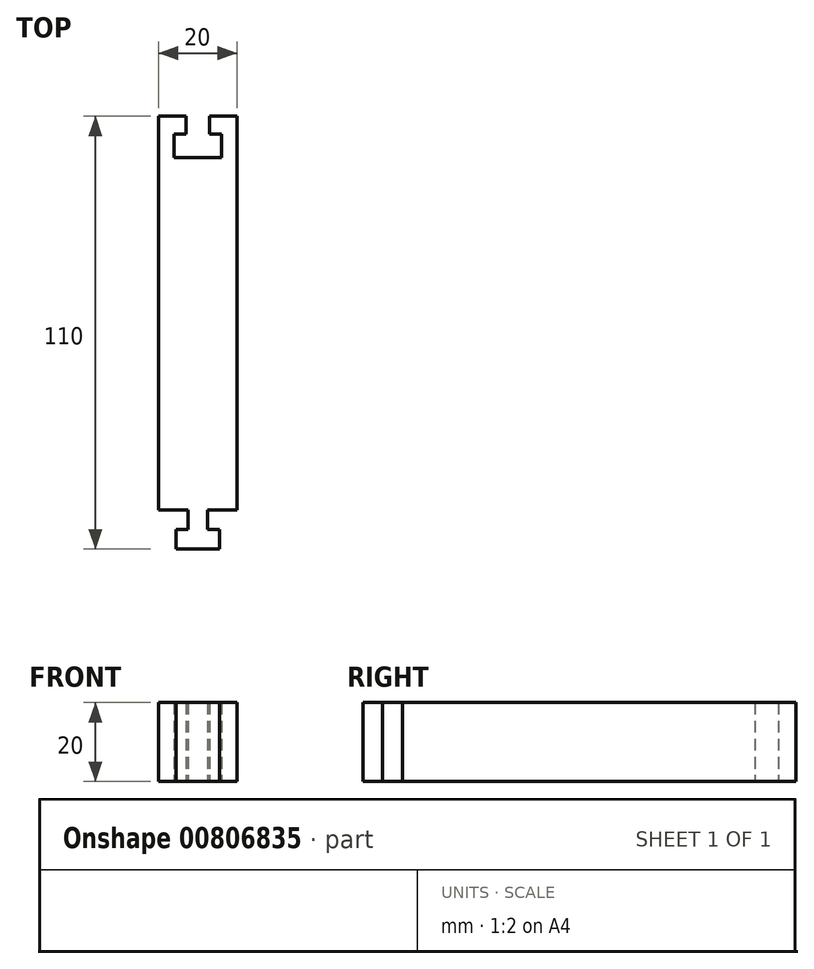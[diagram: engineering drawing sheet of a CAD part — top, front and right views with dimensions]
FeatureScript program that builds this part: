
annotation { "Feature Type Name" : "Feature", "Feature Type Description" : "" }
export const myFeature = defineFeature(function(context is Context, id is Id, definition is map)
    precondition{}
    {
        {
            var Q0;
            Q0=qCreatedBy(makeId("Top.planeOp"),FACE);
            var sketch = newSketch(context, id + "F0", { "sketchPlane" : qUnion([Q0])});
            skLineSegment(sketch, "E0.bottom", {"start": v(10, 50) * mm, "end": v(-10, 50) * mm});
            skLineSegment(sketch, "E0.top", {"start": v(10, -50) * mm, "end": v(-10, -50) * mm});
            skLineSegment(sketch, "E0.left", {"start": v(10, 50) * mm, "end": v(10, -50) * mm});
            skLineSegment(sketch, "E0.right", {"start": v(-10, 50) * mm, "end": v(-10, -50) * mm});
            skPoint(sketch, "E0.middle", {"position": v(0, 0) * mm});
            skLineSegment(sketch, "E1.bottom", {"start": v(3, 42.5) * mm, "end": v(-3, 42.5) * mm});
            skLineSegment(sketch, "E1.top", {"start": v(3, 57.5) * mm, "end": v(-3, 57.5) * mm});
            skLineSegment(sketch, "E1.left", {"start": v(3, 42.5) * mm, "end": v(3, 57.5) * mm});
            skLineSegment(sketch, "E1.right", {"start": v(-3, 42.5) * mm, "end": v(-3, 57.5) * mm});
            skPoint(sketch, "E1.middle", {"position": v(0, 50) * mm});
            skPoint(sketch, "E2.middle", {"position": v(0, -50) * mm});
            skLineSegment(sketch, "E3.bottom", {"start": v(-10, 50) * mm, "end": v(10, 50) * mm});
            skLineSegment(sketch, "E3.left", {"start": v(-10, 50) * mm, "end": v(-10, 35) * mm});
            skLineSegment(sketch, "E3.right", {"start": v(10, 50) * mm, "end": v(10, 35) * mm});
            skLineSegment(sketch, "E4.bottom", {"start": v(-10, -50) * mm, "end": v(10, -50) * mm});
            skLineSegment(sketch, "E4.left", {"start": v(-10, -50) * mm, "end": v(-10, -32.12) * mm});
            skLineSegment(sketch, "E4.right", {"start": v(10, -50) * mm, "end": v(10, -32.12) * mm});
            skLineSegment(sketch, "E5.bottom", {"start": v(6, 39.5) * mm, "end": v(-6, 39.5) * mm});
            skLineSegment(sketch, "E5.top", {"start": v(6, 45.5) * mm, "end": v(-6, 45.5) * mm});
            skLineSegment(sketch, "E5.left", {"start": v(6, 39.5) * mm, "end": v(6, 45.5) * mm});
            skLineSegment(sketch, "E5.right", {"start": v(-6, 39.5) * mm, "end": v(-6, 45.5) * mm});
            skPoint(sketch, "E5.middle", {"position": v(0, 42.5) * mm});
            skLineSegment(sketch, "E6.top", {"start": v(-10, 39.5) * mm, "end": v(10, 39.5) * mm});
            skLineSegment(sketch, "E6.left", {"start": v(-10, 50) * mm, "end": v(-10, 39.5) * mm});
            skLineSegment(sketch, "E6.right", {"start": v(10, 50) * mm, "end": v(10, 39.5) * mm});
            skLineSegment(sketch, "E7.left", {"start": v(-10, -50) * mm, "end": v(-10, -39.5) * mm});
            skLineSegment(sketch, "E7.right", {"start": v(10, -50) * mm, "end": v(10, -39.5) * mm});
            skLineSegment(sketch, "E8.bottom", {"start": v(-5.75, -50) * mm, "end": v(5.75, -50) * mm});
            skLineSegment(sketch, "E9.bottom", {"start": v(2.5, -57.5) * mm, "end": v(-2.5, -57.5) * mm});
            skLineSegment(sketch, "E9.top", {"start": v(2.5, -42.5) * mm, "end": v(-2.5, -42.5) * mm});
            skLineSegment(sketch, "E9.left", {"start": v(2.5, -57.5) * mm, "end": v(2.5, -42.5) * mm});
            skLineSegment(sketch, "E9.right", {"start": v(-2.5, -57.5) * mm, "end": v(-2.5, -42.5) * mm});
            skLineSegment(sketch, "E10.bottom", {"start": v(5.5, -60) * mm, "end": v(-5.5, -60) * mm});
            skLineSegment(sketch, "E10.top", {"start": v(5.5, -55) * mm, "end": v(-5.5, -55) * mm});
            skLineSegment(sketch, "E10.left", {"start": v(5.5, -60) * mm, "end": v(5.5, -55) * mm});
            skLineSegment(sketch, "E10.right", {"start": v(-5.5, -60) * mm, "end": v(-5.5, -55) * mm});
            skPoint(sketch, "E10.middle", {"position": v(0, -57.5) * mm});
            skSolve(sketch);
        }
        {
            var Q0;
            Q0=makeQuery(id+"F0.imprint","IMPRINT",FACE,{"disambiguationData":[TD([[makeQuery(id+"F0.imprint","IMPRINT",EDGE,{"derivedFrom":sQuery(id+"F0.wireOp",EDGE,"E0.left")}),-1.0]])]});
            var Q1;
            {var subQ4=sQuery(id+"F0.wireOp",EDGE,"E5.left");Q1=makeQuery(id+"F0.imprint","IMPRINT",FACE,{"disambiguationData":[TD([[makeQuery(id+"F0.imprint","IMPRINT",EDGE,{"derivedFrom":subQ4}),-1.0]])]});}
            var Q2;
            {var subQ4=sQuery(id+"F0.wireOp",EDGE,"E5.right");Q2=makeQuery(id+"F0.imprint","IMPRINT",FACE,{"disambiguationData":[TD([[makeQuery(id+"F0.imprint","IMPRINT",EDGE,{"derivedFrom":subQ4}),1.0]])]});}
            var Q3;
            {var subQ0=sQuery(id+"F0.wireOp",EDGE,"E9.top");Q3=makeQuery(id+"F0.imprint","IMPRINT",FACE,{"disambiguationData":[TD([[makeQuery(id+"F0.imprint","IMPRINT",EDGE,{"derivedFrom":subQ0}),1.0]])]});}
            var Q4;
            {var subQ0=sQuery(id+"F0.wireOp",EDGE,"E10.top");var subQ1=sQuery(id+"F0.wireOp",EDGE,"E9.left");var subQ2=makeQuery(id+"F0.imprint","INTERSECT",VERTEX,{"derivedFrom":[subQ1,subQ0]});Q4=makeQuery(id+"F0.imprint","IMPRINT",FACE,{"disambiguationData":[TD([[makeQuery(id+"F0.imprint","IMPRINT",EDGE,{"disambiguationData":[TD([[subQ2,-1.0]])],"derivedFrom":subQ1}),1.0]])]});}
            var Q5;
            {var subQ0=sQuery(id+"F0.wireOp",EDGE,"E9.bottom");Q5=makeQuery(id+"F0.imprint","IMPRINT",FACE,{"disambiguationData":[TD([[makeQuery(id+"F0.imprint","IMPRINT",EDGE,{"derivedFrom":subQ0}),-1.0]])]});}
            var Q6;
            {var subQ1=sQuery(id+"F0.wireOp",EDGE,"E9.bottom");Q6=makeQuery(id+"F0.imprint","IMPRINT",FACE,{"disambiguationData":[TD([[makeQuery(id+"F0.imprint","IMPRINT",EDGE,{"derivedFrom":subQ1}),1.0]])]});}
            extrude(context, id + "F1", {"entities" : qUnion([Q0, Q1, Q2, Q3, Q4, Q5, Q6]), "depth" : 20 * mm, "offsetDistance" : 25 * mm});
        }
    });
